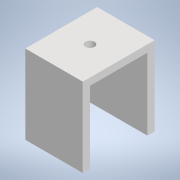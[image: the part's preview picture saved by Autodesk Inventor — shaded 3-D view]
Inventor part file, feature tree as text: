
AUTODESK INVENTOR PART (.ipt)
format: ipt  version: 2020.3 (Build 243373000, 373)  size: 153,088 bytes
history: native  units: mm
features: sketch x7, extrude x7, projected_geometry x3, plane x1
ambient origin geometry x8: Origin, YZ Plane, XZ Plane, XY Plane, X Axis, Y Axis, Z Axis, Center Point
bodies: Solid1 (feature_tree)
feature tree (18):
  sketch  "Sketch1"  dims[d0=20.0mm d1=50.0mm]
  plane  "Work Plane1"
  extrude  "Extrusion2"  Depth=50.0mm
  extrude  "Extrusion3"  Depth=5.0mm TaperAngle=0.0deg
  extrude  "Extrusion4"  Depth=5.0mm TaperAngle=0.0deg
  extrude  "Extrusion5"  Depth=5.0mm
  extrude  "Extrusion6"  Depth=10.0mm
  extrude  "Extrusion7"  Depth=10.0mm
  extrude  "Extrusion8"  Depth=5.0mm
  sketch  "Sketch2"  dims[d4=40.0mm d5=5.0mm d6=0.0mm]
  sketch  "Sketch3"  dims[d7=5.0mm d8=0.0mm d9=5.0mm d10=0.0mm]
  projected_geometry  "Projected Loop1"
  projected_geometry  "Projected Loop2"
  sketch  "Sketch4"  dims[d11=5.0mm d12=0.0mm d13=5.2mm]
  projected_geometry  "Projected Loop3"
  sketch  "Sketch5"  dims[d14=10.0mm d15=0.0mm d16=10.0mm]
  sketch  "Sketch6"  dims[d17=50.0mm d18=10.0mm]
  sketch  "Sketch7"  dims[d19=5.0mm d20=0.0mm d21=5.0mm d22=50.0mm d23=0.0mm]
